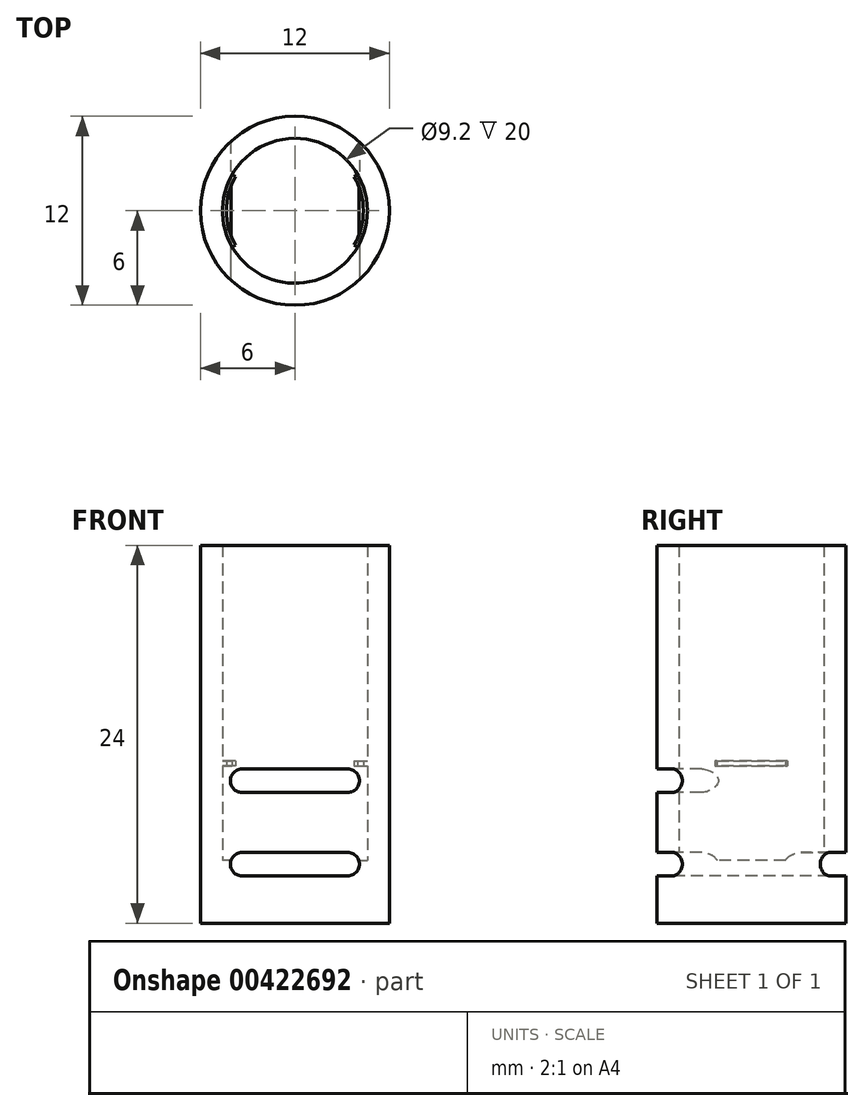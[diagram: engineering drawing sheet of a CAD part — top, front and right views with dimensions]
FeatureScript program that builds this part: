
annotation { "Feature Type Name" : "Feature", "Feature Type Description" : "" }
export const myFeature = defineFeature(function(context is Context, id is Id, definition is map)
    precondition{}
    {
        {
            var Q0;
            Q0=qCreatedBy(makeId("Top.planeOp"),FACE);
            var sketch = newSketch(context, id + "F0", { "sketchPlane" : qUnion([Q0])});
            skCircle(sketch, "E0", {"center": v(0, 0) * mm, "radius": 6 * mm});
            skSolve(sketch);
        }
        {
            var Q0;
            Q0=qSketchRegion(id+"F0",true);
            extrude(context, id + "F1", {"entities" : qUnion([Q0]), "depth" : 4 * mm});
        }
        {
            var Q0;
            Q0=makeQuery(id+"F1.opExtrude","CAP_FACE",FACE,{"disambiguationData":[OSD([sQuery(id+"F0.wireOp",EDGE,"E0")])],"isStart":false});
            var sketch = newSketch(context, id + "F2", { "sketchPlane" : qUnion([Q0])});
            skCircle(sketch, "E1", {"center": v(0, 0) * mm, "radius": 4.6 * mm});
            skSolve(sketch);
        }
        {
            var Q0;
            Q0=makeQuery(id+"F2.imprint","IMPRINT",FACE,{"disambiguationData":[TD([[makeQuery(id+"F2.imprint","IMPRINT",EDGE,{"derivedFrom":sQuery(id+"F2.wireOp",EDGE,"E1")}),-1.0]])]});
            extrude(context, id + "F3", {"entities" : qUnion([Q0]), "operationType" : NewBodyOperationType.ADD, "depth" : 20 * mm});
        }
        {
            var Q0;
            Q0=qCreatedBy(makeId("Front.planeOp"),FACE);
            cPlane(context, id + "F4", {"entities" : qUnion([Q0]), "cplaneType" : CPlaneType.OFFSET, "offset" : 10 * mm, "width" : 150 * mm, "height" : 150 * mm});
        }
        {
            var Q0;
            Q0=qCreatedBy(id+"F4.planeOp",FACE);
            var sketch = newSketch(context, id + "F5", { "sketchPlane" : qUnion([Q0])});
            skLineSegment(sketch, "E2.bottom", {"start": v(-3.35, 4.5) * mm, "end": v(3.35, 4.5) * mm});
            skLineSegment(sketch, "E2.top", {"start": v(-3.35, 3) * mm, "end": v(3.35, 3) * mm});
            skLineSegment(sketch, "E2.left", {"start": v(-3.35, 4.5) * mm, "end": v(-3.35, 3) * mm});
            skLineSegment(sketch, "E2.right", {"start": v(3.35, 4.5) * mm, "end": v(3.35, 3) * mm});
            skLineSegment(sketch, "E3", {"start": v(0, 0) * mm, "end": v(0, 11.71) * mm, "construction": true});
            skPoint(sketch, "E4", {"position": v(0, 3) * mm});
            skCircle(sketch, "E5", {"center": v(3.35, 3.75) * mm, "radius": 0.75 * mm});
            skCircle(sketch, "E6", {"center": v(-3.35, 3.75) * mm, "radius": 0.75 * mm});
            skSolve(sketch);
        }
        {
            var Q0;
            Q0=qSketchRegion(id+"F5",true);
            extrude(context, id + "F6", {"entities" : qUnion([Q0]), "operationType" : NewBodyOperationType.REMOVE, "oppositeDirection" : true, "depth" : 25 * mm});
        }
        {
            var Q0;
            Q0=makeQuery(id+"F1.opExtrude","CAP_FACE",FACE,{"disambiguationData":[OSD([sQuery(id+"F0.wireOp",EDGE,"E0")])],"isStart":true});
            cPlane(context, id + "F7", {"entities" : qUnion([Q0]), "cplaneType" : CPlaneType.OFFSET, "offset" : 10 * mm, "oppositeDirection" : true, "width" : 150 * mm, "height" : 150 * mm});
        }
        {
            var Q0;
            Q0=qCreatedBy(id+"F7.planeOp",FACE);
            var sketch = newSketch(context, id + "F8", { "sketchPlane" : qUnion([Q0])});
            skArc(sketch, "E7", {"start": v(-3.77, 2.17) * mm, "mid": v(-4.35, 0) * mm, "end": v(-3.77, -2.18) * mm});
            skArc(sketch, "E8", {"start": v(3.98, -2.3) * mm, "mid": v(4.6, 0) * mm, "end": v(3.98, 2.3) * mm});
            skLineSegment(sketch, "E9", {"start": v(0, 0) * mm, "end": v(0, -1.7) * mm, "construction": true});
            skLineSegment(sketch, "E10", {"start": v(-3.77, -2.18) * mm, "end": v(-3.98, -2.3) * mm});
            skLineSegment(sketch, "E11", {"start": v(-3.77, 2.18) * mm, "end": v(-3.98, 2.3) * mm});
            skArc(sketch, "E12.MirrorCS", {"start": v(3.77, 2.17) * mm, "mid": v(4.35, 0) * mm, "end": v(3.77, -2.18) * mm});
            skLineSegment(sketch, "E13.MirrorCS", {"start": v(3.77, -2.18) * mm, "end": v(3.98, -2.3) * mm});
            skLineSegment(sketch, "E14.MirrorCS", {"start": v(3.77, 2.18) * mm, "end": v(3.98, 2.3) * mm});
            skArc(sketch, "E15.trimOffspring", {"start": v(-3.98, 2.3) * mm, "mid": v(-4.6, 0) * mm, "end": v(-3.98, -2.3) * mm});
            skSolve(sketch);
        }
        {
            var Q0;
            Q0=qSketchRegion(id+"F8",true);
            extrude(context, id + "F9", {"entities" : qUnion([Q0]), "operationType" : NewBodyOperationType.ADD, "oppositeDirection" : true, "depth" : 0.3 * mm});
        }
        {
            var Q0;
            Q0=qCreatedBy(id+"F4.planeOp",FACE);
            var sketch = newSketch(context, id + "F10", { "sketchPlane" : qUnion([Q0])});
            skLineSegment(sketch, "E16.bottom", {"start": v(-3.35, 9.8) * mm, "end": v(3.35, 9.8) * mm});
            skLineSegment(sketch, "E16.top", {"start": v(-3.35, 8.3) * mm, "end": v(3.35, 8.3) * mm});
            skLineSegment(sketch, "E16.left", {"start": v(-3.35, 9.8) * mm, "end": v(-3.35, 8.3) * mm});
            skLineSegment(sketch, "E16.right", {"start": v(3.35, 9.8) * mm, "end": v(3.35, 8.3) * mm});
            skLineSegment(sketch, "E17", {"start": v(0, 5.3) * mm, "end": v(0, 17.01) * mm, "construction": true});
            skPoint(sketch, "E18", {"position": v(0, 8.3) * mm});
            skCircle(sketch, "E19", {"center": v(3.35, 9.05) * mm, "radius": 0.75 * mm});
            skCircle(sketch, "E20", {"center": v(-3.35, 9.05) * mm, "radius": 0.75 * mm});
            skSolve(sketch);
        }
        {
            var Q0;
            Q0 = qSketchRegion(id + "F10", true);
            extrude(context, id + "F11", {"entities" : qUnion([Q0]), "operationType" : NewBodyOperationType.REMOVE, "oppositeDirection" : true, "depth" : 10 * mm});
        }
    });
